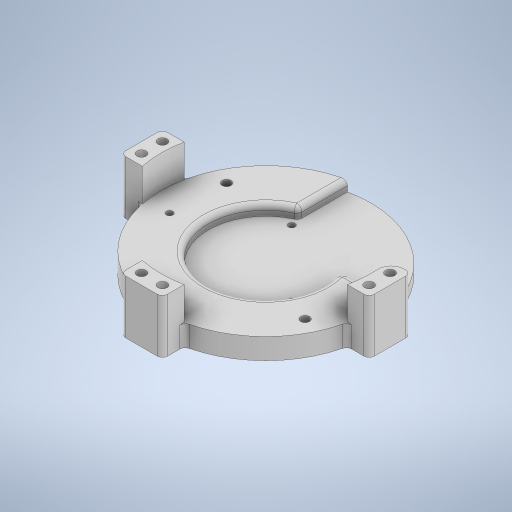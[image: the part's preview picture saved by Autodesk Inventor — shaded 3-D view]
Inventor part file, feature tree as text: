
AUTODESK INVENTOR PART (.ipt)
format: ipt  version: 2023 (Build 270158000, 158)  size: 478,720 bytes
history: native  units: in
note: dims shown in document units (in); Inventor stores cm internally (conversion verified against a paired STEP export)
features: sketch x14, extrude x10, fillet x5, hole x3
ambient origin geometry x8: Origin, YZ Plane, XZ Plane, XY Plane, X Axis, Y Axis, Z Axis, Center Point
bodies: Solid1 (feature_tree)
feature tree (32):
  extrude  "Extrusion1"  Depth=0.2in TaperAngle=0.0deg
  extrude  "Extrusion2"  Depth=0.2in TaperAngle=0.0deg
  extrude  "Extrusion3"  Depth=0.5in
  extrude  "Extrusion4"  Depth=0.4in
  fillet  "Fillet1"  Radius=0.5in
  fillet  "Fillet2"  Radius=0.5in
  fillet  "Fillet3"  Radius=0.4in
  extrude  "Extrusion5"  Depth=0.4in TaperAngle=0.0deg
  extrude  "Extrusion6"  Depth=0.2in
  extrude  "Extrusion7"  Depth=0.2in
  extrude  "Extrusion8"  Depth=0.2in
  fillet  "Fillet4"  Radius=0.2in
  extrude  "Extrusion9"  Depth=0.4in
  sketch  "Sketch10"  dims[d33=0.177in d34=0.177in]
  hole  "Hole1"  [1 undecoded]
  extrude  "Extrusion10"  Depth=5.0in TaperAngle=0.0deg
  hole  "Hole2"  [1 undecoded]
  fillet  "Fillet5"  Radius=0.1in
  hole  "Hole3"  [1 undecoded]
  sketch  "Sketch1"  dims[d0=4.0in d1=0.2in d2=0.0in]
  sketch  "Sketch2"  dims[d3=2.2in d4=0.2in d5=0.0in]
  sketch  "Sketch3"  dims[d6=3.75in d10=0.5in]
  sketch  "Sketch4"  dims[d11=0.4in d12=0.4in d13=0.5in d14=0.5in d15=0.4in]
  sketch  "Sketch5"  dims[d16=0.4in d17=1.025in d18=0.0in]
  sketch  "Sketch6"  dims[d19=0.2in d20=0.2in]
  sketch  "Sketch7"  dims[d21=0.4in d22=0.2in]
  sketch  "Sketch8"  dims[d23=0.4in d24=0.2in d25=0.2in]
  sketch  "Sketch9"  dims[d26=0.4in d30=0.177in]
  sketch  "Sketch11"  dims[d35=0.177in d36=5.0in d37=0.0in]
  sketch  "Sketch12"  dims[d38=0.1in d39=0.1in d40=0.1in]
  sketch  "Sketch13"  dims[d41=0.2in d42=0.0in d43=0.625in d44=0.0in]
  sketch  "Sketch14"  dims[d45=0.2in d46=0.0in d47=0.3in d48=0.3in d49=0.3in d50=0.3in d51=0.3in d52=0.2in d53=0.0in d54=0.1in d55=0.7in d56=0.8875in d57=0.8875in d58=0.25in d59=0.25in d60=0.2in d61=0.0in d62=0.126in d63=0.432in d64=0.256in d65=0.118in d66=90.0deg d67=0.5in d68=0.8108in d69=1.65in d70=45.0deg d71=1.65in d72=45.0deg d73=0.25in d74=0.2in d75=0.0in d76=0.126in d77=0.75in d78=0.375in d79=0.25in d80=0.5635in d81=1.0in d82=0.8108in d83=0.25in d84=0.4154in d85=0.2in d86=1.5in d87=0.75in d88=1.5in d89=0.75in d90=0.169in d91=0.75in d92=0.315in d93=0.157in d94=0.5635in d95=1.0in d96=0.8108in]
note: 3 required parameter values undecoded (feature->parameter linkage not recoverable at this tier; creation-order binding heuristic only, values carry confidence <= 0.55)
